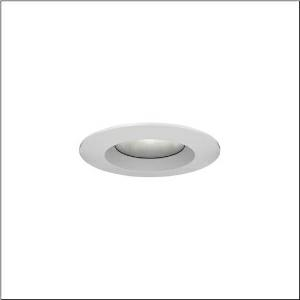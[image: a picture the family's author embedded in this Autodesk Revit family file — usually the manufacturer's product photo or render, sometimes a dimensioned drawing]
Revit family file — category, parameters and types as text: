
# Revit family: lunis_40_ip65_5dp10c72v365
name_source: partatom
category: Lighting Fixtures
units: mm (PartAtom-declared; Revit-internal decimal feet)

## family parameters
Cut with Voids When Loaded = No
Host = Face
Light Source = No
Part Type = Normal
Room Calculation Point = No
Round Connector Dimension = Use Diameter
Shared = No

## types (1)
- Lunis 40 IP65 (1 x LED, 350 lm, 3.5 W, 3000K)
    Apparent Load = 4 VA
    CIE Flux Codes = 57 88 99 100 100
    Color Rendering = 80
    Color Temperature = 3000K
    Default Elevation = 1800 mm
    Description = Lunis 40 IP65, downlight, of PMMA, light emission: direct distribution, LED rated luminous flux: 350lm, light colour: 830, control gear: ECG, mains connection: 220..240V, AC, 50/60Hz, housing, round, of aluminium, coated, traffic white (RAL 9016), diameter: 83mm, recess depth: 43mm, protection rating (complete): IP20, insulation class (complete): insulation class II (safety insulation), certification: CE, permissible ambient temperature for indoor applications: -20..+40°C, packaging unit: 1 piece
    Height = 0 mm  [stored 0 ft]
    Lamp = 1 x LED
    Lamp Light Flux = 350 lm
    Lamp Power = 3.5 W
    Lamp count = 1
    Length = 83 mm
    Luminous efficacy = 100 lm/W
    Manufacturer = Siteco
    ModVariant = No
    Model = 5DP10C72V365
    Mounting Place = Ceiling
    Mounting Type = Recessed
    Number of Poles = 1
    OnlyDefault = Yes
    Power Factor = 1
    Product Name = Lunis 40 IP65
    Product group = downlight | ceiling recessed
    ProductGroupID = 402
    Protection Class = Protection class II
    Protection Degree = IP 20
    RLX_Detail_Level = 1
    RlxData = <blob elided: 24069 chars, md5=c30cb43b>
    Socket = socket
    Standby Power = 0 W
    System Light Flux = 350 lm
    System Power = 4 W
    Type Comments = Product without accessories
    Type Image = l_1006628.jpg
    URL = http://relux.com
    VarID = ---
    Voltage = 0 V
    Weight = 0.00 kg
    Width = 0 mm  [stored 0 ft]

note: [stored X ft] marks values corroborated as IEEE doubles in the binary element streams (Revit-internal decimal feet)

## geometry (parser evidence)
native form markers: Blend x4, Sweep x11
no freeform markers — native parametric forms only
